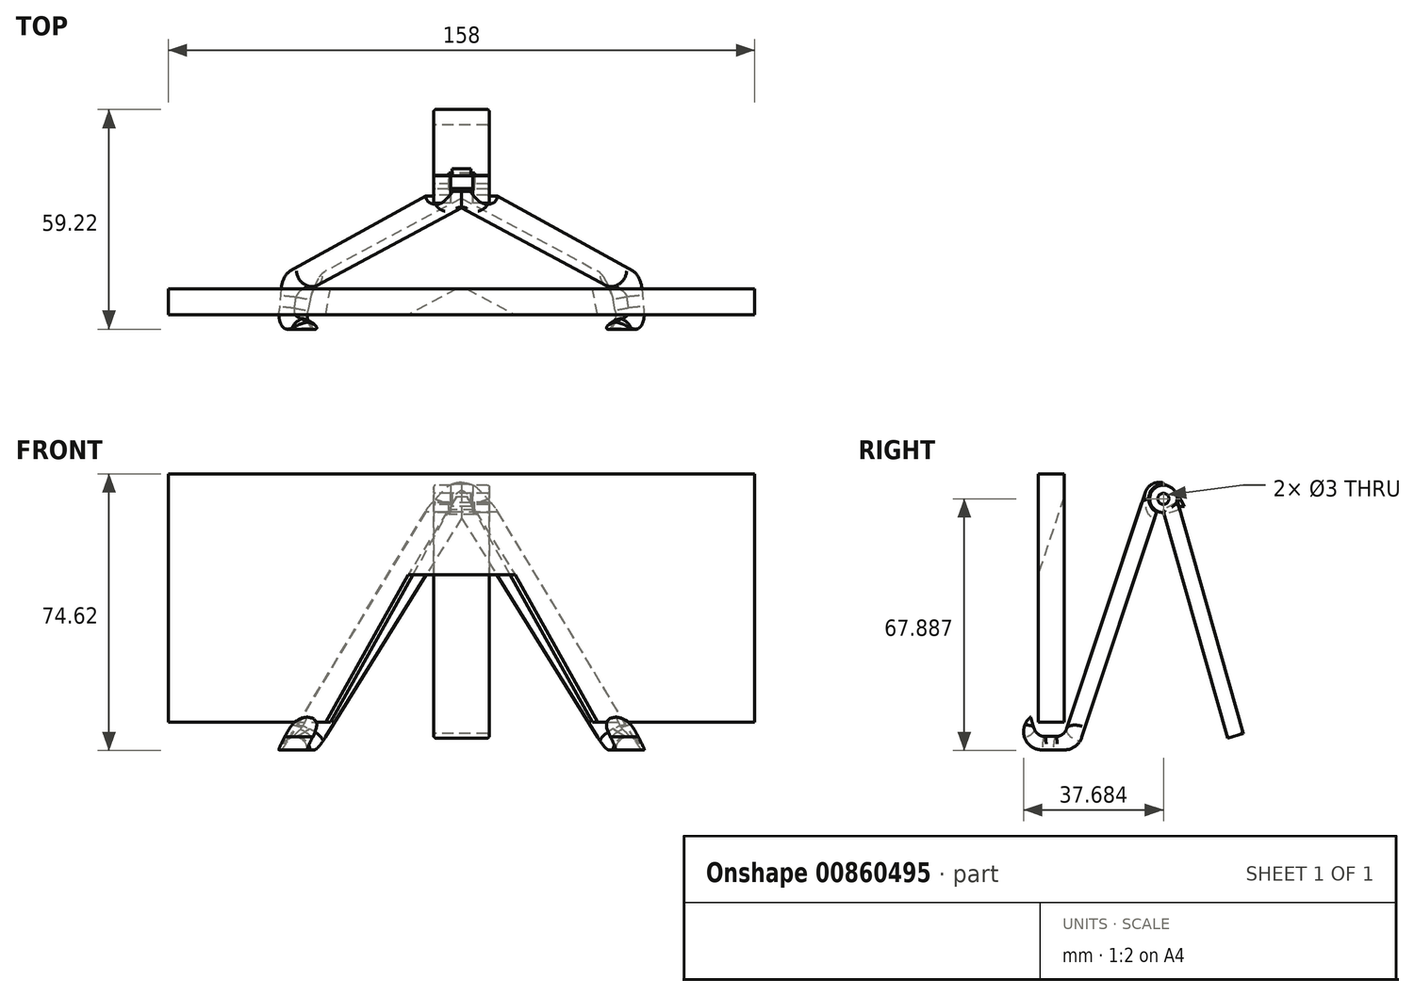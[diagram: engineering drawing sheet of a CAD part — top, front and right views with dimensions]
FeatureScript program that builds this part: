
annotation { "Feature Type Name" : "Feature", "Feature Type Description" : "" }
export const myFeature = defineFeature(function(context is Context, id is Id, definition is map)
    precondition{}
    {
        {
            var Q0;
            Q0=qCreatedBy(makeId("Front.planeOp"),FACE);
            var sketch = newSketch(context, id + "F0", { "sketchPlane" : qUnion([Q0])});
            skLineSegment(sketch, "E0.bottom", {"start": v(-79, 33.5) * mm, "end": v(79, 33.5) * mm});
            skLineSegment(sketch, "E0.top", {"start": v(-79, -33.5) * mm, "end": v(79, -33.5) * mm});
            skLineSegment(sketch, "E0.left", {"start": v(-79, 33.5) * mm, "end": v(-79, -33.5) * mm});
            skLineSegment(sketch, "E0.right", {"start": v(79, 33.5) * mm, "end": v(79, -33.5) * mm});
            skPoint(sketch, "E0.middle", {"position": v(0, 0) * mm});
            skSolve(sketch);
        }
        {
            var Q0;
            Q0=makeQuery(id+"F0.imprint","IMPRINT",FACE,{"disambiguationData":[TD([[makeQuery(id+"F0.imprint","IMPRINT",EDGE,{"derivedFrom":sQuery(id+"F0.wireOp",EDGE,"E0.bottom")}),-1.0]])]});
            extrude(context, id + "F1", {"entities" : qUnion([Q0]), "depth" : 7 * mm, "offsetDistance" : 25 * mm});
        }
        {
            var Q0;
            Q0=qCreatedBy(makeId("Right.planeOp"),FACE);
            var sketch = newSketch(context, id + "F2", { "sketchPlane" : qUnion([Q0])});
            skLineSegment(sketch, "E1", {"start": v(-9.07, -31.74) * mm, "end": v(-7.37, -37.3) * mm});
            skLineSegment(sketch, "E2", {"start": v(-7.37, -37.3) * mm, "end": v(0, -37.3) * mm});
            skLineSegment(sketch, "E3", {"start": v(0, -37.3) * mm, "end": v(22.96, 31.77) * mm});
            skLineSegment(sketch, "E4", {"start": v(-9.07, -31.74) * mm, "end": v(-12.14, -32.68) * mm});
            skLineSegment(sketch, "E5", {"start": v(-12.14, -32.68) * mm, "end": v(-9.6, -40.94) * mm});
            skLineSegment(sketch, "E6", {"start": v(-9.6, -40.94) * mm, "end": v(3.65, -40.94) * mm});
            skLineSegment(sketch, "E7", {"start": v(3.65, -40.94) * mm, "end": v(27.56, 30.98) * mm});
            skLineSegment(sketch, "E8", {"start": v(27.56, 30.98) * mm, "end": v(22.96, 31.77) * mm});
            skLineSegment(sketch, "E9", {"start": v(-7.37, -37.3) * mm, "end": v(-9.6, -40.94) * mm});
            skLineSegment(sketch, "E10", {"start": v(3.97, -25.36) * mm, "end": v(7.92, -28.08) * mm});
            skSolve(sketch);
        }
        {
            var Q0;
            {var subQ0=sQuery(id+"F2.wireOp",EDGE,"E8");Q0=makeQuery(id+"F2.imprint","IMPRINT",FACE,{"disambiguationData":[TD([[makeQuery(id+"F2.imprint","IMPRINT",EDGE,{"derivedFrom":subQ0}),1.0]])]});}
            var Q1;
            Q1=makeQuery(id+"F2.imprint","IMPRINT",FACE,{"disambiguationData":[TD([[makeQuery(id+"F2.imprint","IMPRINT",EDGE,{"derivedFrom":sQuery(id+"F2.wireOp",EDGE,"E1")}),-1.0]])]});
            var Q2;
            {var subQ4=sQuery(id+"F2.wireOp",EDGE,"E2");Q2=makeQuery(id+"F2.imprint","IMPRINT",FACE,{"disambiguationData":[TD([[makeQuery(id+"F2.imprint","IMPRINT",EDGE,{"derivedFrom":subQ4}),-1.0]])]});}
            extrude(context, id + "F3", {"entities" : qUnion([Q0, Q1, Q2]), "endBound" : BoundingType.SYMMETRIC, "depth" : 100 * mm, "offsetDistance" : 25 * mm});
        }
        {
            var Q0;
            Q0=makeQuery(id+"F3.opExtrude","SWEPT_FACE",FACE,{"disambiguationData":[OSD([sQuery(id+"F2.wireOp",EDGE,"E7")])]});
            var sketch = newSketch(context, id + "F4", { "sketchPlane" : qUnion([Q0])});
            skLineSegment(sketch, "E11", {"start": v(0, 0) * mm, "end": v(0, 28.2) * mm});
            skPoint(sketch, "E11.endSnap0", {"position": v(0, 38.1) * mm});
            skLineSegment(sketch, "E12", {"start": v(0, 28.2) * mm, "end": v(42.66, -44.2) * mm});
            skLineSegment(sketch, "E13", {"start": v(42.66, -44.2) * mm, "end": v(0, -44.2) * mm});
            skLineSegment(sketch, "E14", {"start": v(0, -44.2) * mm, "end": v(0, 0) * mm});
            skLineSegment(sketch, "E15.MirrorCS", {"start": v(0, 28.2) * mm, "end": v(-42.66, -44.2) * mm});
            skLineSegment(sketch, "E16.MirrorCS", {"start": v(-42.66, -44.2) * mm, "end": v(0, -44.2) * mm});
            skSolve(sketch);
        }
        {
            var Q0;
            {var subQ0=sQuery(id+"F4.wireOp",EDGE,"E11");Q0=makeQuery(id+"F4.imprint","IMPRINT",FACE,{"disambiguationData":[TD([[makeQuery(id+"F4.imprint","IMPRINT",EDGE,{"derivedFrom":subQ0}),1.0]])]});}
            var Q1;
            {var subQ0=sQuery(id+"F4.wireOp",EDGE,"E11");Q1=makeQuery(id+"F4.imprint","IMPRINT",FACE,{"disambiguationData":[TD([[makeQuery(id+"F4.imprint","IMPRINT",EDGE,{"derivedFrom":subQ0}),-1.0]])]});}
            var Q2;
            {var subQ0=sQuery(id+"F4.wireOp",EDGE,"E13");Q2=makeQuery(id+"F4.imprint","IMPRINT",FACE,{"disambiguationData":[TD([[makeQuery(id+"F4.imprint","IMPRINT",EDGE,{"derivedFrom":subQ0}),-1.0]])]});}
            var Q3;
            {var subQ0=sQuery(id+"F4.wireOp",EDGE,"E16.MirrorCS");Q3=makeQuery(id+"F4.imprint","IMPRINT",FACE,{"disambiguationData":[TD([[makeQuery(id+"F4.imprint","IMPRINT",EDGE,{"derivedFrom":subQ0}),1.0]])]});}
            extrude(context, id + "F5", {"entities" : qUnion([Q0, Q1, Q2, Q3]), "operationType" : NewBodyOperationType.REMOVE, "oppositeDirection" : true, "depth" : 25 * mm, "offsetDistance" : 25 * mm});
        }
        {
            var Q0;
            Q0=makeQuery(id+"F3.opExtrude","CAP_EDGE",EDGE,{"disambiguationData":[OSD([sQuery(id+"F2.wireOp",EDGE,"E8")])],"isStart":true});
            var Q1;
            Q1=makeQuery(id+"F3.opExtrude","CAP_EDGE",EDGE,{"disambiguationData":[OSD([sQuery(id+"F2.wireOp",EDGE,"E8")])],"isStart":false});
            chamfer(context, id + "F6", {"entities" : qUnion([Q0, Q1]), "chamferType" : ChamferType.OFFSET_ANGLE, "width" : 45 * mm, "oppositeDirection" : false, "angle" : 60 * degree, "tangentPropagation" : true});
        }
        {
            var Q0;
            {var subQ0=sQuery(id+"F2.wireOp",EDGE,"E8");Q0=makeQuery(id+"F6.opChamfer","BLEND_EDGE",EDGE,{"blendedFrom":[makeQuery(id+"F3.opExtrude","CAP_EDGE",EDGE,{"disambiguationData":[OSD([subQ0])],"isStart":true}),makeQuery(id+"F3.opExtrude","SWEPT_FACE",FACE,{"disambiguationData":[OSD([subQ0])]})],"blendedInto":[makeQuery(id+"F3.opExtrude","SWEPT_FACE",FACE,{"disambiguationData":[OSD([subQ0])]})]});}
            var Q1;
            {var subQ0=sQuery(id+"F2.wireOp",EDGE,"E8");Q1=makeQuery(id+"F6.opChamfer","BLEND_EDGE",EDGE,{"blendedFrom":[makeQuery(id+"F3.opExtrude","CAP_EDGE",EDGE,{"disambiguationData":[OSD([subQ0])],"isStart":false}),makeQuery(id+"F3.opExtrude","SWEPT_FACE",FACE,{"disambiguationData":[OSD([subQ0])]})],"blendedInto":[makeQuery(id+"F3.opExtrude","SWEPT_FACE",FACE,{"disambiguationData":[OSD([subQ0])]})]});}
            fillet(context, id + "F7", {"entities" : qUnion([Q0, Q1]), "radius" : 10 * mm, "tangentPropagation" : true, "allowEdgeOverflow" : false});
        }
        {
            var Q0;
            Q0=qCreatedBy(makeId("Right.planeOp"),FACE);
            var sketch = newSketch(context, id + "F8", { "sketchPlane" : qUnion([Q0])});
            skCircle(sketch, "E17", {"center": v(26.8, 26.76) * mm, "radius": 1.5 * mm});
            skCircle(sketch, "E18.0", {"center": v(26.8, 26.76) * mm, "radius": 4 * mm});
            skLineSegment(sketch, "E19", {"start": v(30.5, 28.26) * mm, "end": v(32.38, 24.7) * mm});
            skLineSegment(sketch, "E20", {"start": v(32.38, 24.7) * mm, "end": v(30.25, 24.73) * mm});
            skSolve(sketch);
        }
        {
            var Q0;
            Q0=makeQuery(id+"F8.imprint","IMPRINT",FACE,{"disambiguationData":[TD([[makeQuery(id+"F8.imprint","IMPRINT",EDGE,{"derivedFrom":sQuery(id+"F8.wireOp",EDGE,"E17")}),-1.0]])]});
            var Q1;
            {var subQ0=sQuery(id+"F8.wireOp",EDGE,"E19");Q1=makeQuery(id+"F8.imprint","IMPRINT",FACE,{"disambiguationData":[TD([[makeQuery(id+"F8.imprint","IMPRINT",EDGE,{"derivedFrom":subQ0}),-1.0]])]});}
            extrude(context, id + "F9", {"entities" : qUnion([Q0, Q1]), "endBound" : BoundingType.SYMMETRIC, "depth" : 5 * mm, "offsetDistance" : 25 * mm});
        }
        {
            var Q0;
            Q0=makeQuery(id+"F8.imprint","IMPRINT",FACE,{"disambiguationData":[TD([[makeQuery(id+"F8.imprint","IMPRINT",EDGE,{"derivedFrom":sQuery(id+"F8.wireOp",EDGE,"E17")}),1.0]])]});
            extrude(context, id + "F10", {"entities" : qUnion([Q0]), "operationType" : NewBodyOperationType.REMOVE, "endBound" : BoundingType.SYMMETRIC, "oppositeDirection" : true, "depth" : 25 * mm, "offsetDistance" : 25 * mm});
        }
        {
            var Q0;
            Q0=qCreatedBy(makeId("Right.planeOp"),FACE);
            var sketch = newSketch(context, id + "F11", { "sketchPlane" : qUnion([Q0])});
            skCircle(sketch, "E21", {"center": v(26.8, 26.77) * mm, "radius": 1.5 * mm});
            skCircle(sketch, "E22.0", {"center": v(26.8, 26.77) * mm, "radius": 3.7 * mm});
            skSolve(sketch);
        }
        {
            var Q0;
            Q0=makeQuery(id+"F8.imprint","IMPRINT",FACE,{"disambiguationData":[TD([[makeQuery(id+"F8.imprint","IMPRINT",EDGE,{"derivedFrom":sQuery(id+"F8.wireOp",EDGE,"E17")}),-1.0]])]});
            extrude(context, id + "F12", {"entities" : qUnion([Q0]), "operationType" : NewBodyOperationType.REMOVE, "endBound" : BoundingType.SYMMETRIC, "depth" : 25 * mm, "offsetDistance" : 25 * mm});
        }
        {
            var Q0;
            Q0=makeQuery(id+"F11.imprint","IMPRINT",FACE,{"disambiguationData":[TD([[makeQuery(id+"F11.imprint","IMPRINT",EDGE,{"derivedFrom":sQuery(id+"F11.wireOp",EDGE,"E21")}),-1.0]])]});
            extrude(context, id + "F13", {"entities" : qUnion([Q0]), "endBound" : BoundingType.SYMMETRIC, "depth" : 15 * mm, "offsetDistance" : 25 * mm});
        }
        {
            var Q0;
            Q0=qCreatedBy(makeId("Right.planeOp"),FACE);
            var sketch = newSketch(context, id + "F14", { "sketchPlane" : qUnion([Q0])});
            skLineSegment(sketch, "E23", {"start": v(26.65, 23.91) * mm, "end": v(44.16, -37.71) * mm});
            skLineSegment(sketch, "E24", {"start": v(44.16, -37.71) * mm, "end": v(48.33, -36.53) * mm});
            skLineSegment(sketch, "E25", {"start": v(48.33, -36.53) * mm, "end": v(30.6, 25.84) * mm});
            skLineSegment(sketch, "E26", {"start": v(26.65, 23.91) * mm, "end": v(30.6, 25.84) * mm});
            skLineSegment(sketch, "E27", {"start": v(31.19, 23.8) * mm, "end": v(27.02, 22.62) * mm});
            skSolve(sketch);
        }
        {
            var Q0;
            Q0=makeQuery(id+"F11.imprint","IMPRINT",FACE,{"disambiguationData":[TD([[makeQuery(id+"F11.imprint","IMPRINT",EDGE,{"derivedFrom":sQuery(id+"F11.wireOp",EDGE,"E21")}),-1.0]])]});
            extrude(context, id + "F15", {"entities" : qUnion([Q0]), "operationType" : NewBodyOperationType.REMOVE, "endBound" : BoundingType.SYMMETRIC, "oppositeDirection" : true, "depth" : 6 * mm, "offsetDistance" : 25 * mm});
        }
        {
            var Q0;
            Q0=makeQuery(id+"F14.imprint","IMPRINT",FACE,{"disambiguationData":[TD([[makeQuery(id+"F14.imprint","IMPRINT",EDGE,{"derivedFrom":sQuery(id+"F14.wireOp",EDGE,"E23")}),1.0]])]});
            extrude(context, id + "F16", {"entities" : qUnion([Q0]), "operationType" : NewBodyOperationType.ADD, "endBound" : BoundingType.SYMMETRIC, "depth" : 15 * mm, "offsetDistance" : 25 * mm});
        }
        {
            var Q0;
            {var subQ0=sQuery(id+"F14.wireOp",EDGE,"E26");Q0=makeQuery(id+"F14.imprint","IMPRINT",FACE,{"disambiguationData":[TD([[makeQuery(id+"F14.imprint","IMPRINT",EDGE,{"derivedFrom":subQ0}),-1.0]])]});}
            extrude(context, id + "F17", {"entities" : qUnion([Q0]), "operationType" : NewBodyOperationType.REMOVE, "endBound" : BoundingType.SYMMETRIC, "depth" : 7 * mm, "offsetDistance" : 25 * mm});
        }
        {
            var Q0;
            {var subQ0=sQuery(id+"F2.wireOp",EDGE,"E8");Q0=makeQuery(id+"F7.opFillet","BLEND_EDGE",EDGE,{"blendedFrom":[makeQuery(id+"F6.opChamfer","BLEND_EDGE",EDGE,{"blendedFrom":[makeQuery(id+"F3.opExtrude","CAP_EDGE",EDGE,{"disambiguationData":[OSD([subQ0])],"isStart":true}),makeQuery(id+"F3.opExtrude","SWEPT_FACE",FACE,{"disambiguationData":[OSD([subQ0])]})],"blendedInto":[makeQuery(id+"F3.opExtrude","SWEPT_FACE",FACE,{"disambiguationData":[OSD([subQ0])]})]}),makeQuery(id+"F3.opExtrude","SWEPT_FACE",FACE,{"disambiguationData":[OSD([sQuery(id+"F2.wireOp",EDGE,"E7")])]})],"blendedInto":[makeQuery(id+"F3.opExtrude","SWEPT_FACE",FACE,{"disambiguationData":[OSD([sQuery(id+"F2.wireOp",EDGE,"E7")])]})]});}
            var Q1;
            {var subQ0=sQuery(id+"F2.wireOp",EDGE,"E8");Q1=makeQuery(id+"F7.opFillet","BLEND_EDGE",EDGE,{"blendedFrom":[makeQuery(id+"F6.opChamfer","BLEND_EDGE",EDGE,{"blendedFrom":[makeQuery(id+"F3.opExtrude","CAP_EDGE",EDGE,{"disambiguationData":[OSD([subQ0])],"isStart":false}),makeQuery(id+"F3.opExtrude","SWEPT_FACE",FACE,{"disambiguationData":[OSD([subQ0])]})],"blendedInto":[makeQuery(id+"F3.opExtrude","SWEPT_FACE",FACE,{"disambiguationData":[OSD([subQ0])]})]}),makeQuery(id+"F3.opExtrude","SWEPT_FACE",FACE,{"disambiguationData":[OSD([sQuery(id+"F2.wireOp",EDGE,"E7")])]})],"blendedInto":[makeQuery(id+"F3.opExtrude","SWEPT_FACE",FACE,{"disambiguationData":[OSD([sQuery(id+"F2.wireOp",EDGE,"E7")])]})]});}
            fillet(context, id + "F18", {"entities" : qUnion([Q0, Q1]), "radius" : 1 * mm, "tangentPropagation" : true, "allowEdgeOverflow" : false});
        }
        {
            var Q0;
            Q0=makeQuery(id+"F16.boolean.opBoolean","MERGE",FACE,{"derivedFrom":[makeQuery(id+"F13.opExtrude","CAP_FACE",FACE,{"disambiguationData":[OSD([sQuery(id+"F11.wireOp",EDGE,"E21"),sQuery(id+"F11.wireOp",EDGE,"E22.0")])],"isStart":true}),makeQuery(id+"F16.opExtrude","CAP_FACE",FACE,{"disambiguationData":[OSD([sQuery(id+"F14.wireOp",EDGE,"E23"),sQuery(id+"F14.wireOp",EDGE,"E24"),sQuery(id+"F14.wireOp",EDGE,"E25"),sQuery(id+"F14.wireOp",EDGE,"E26")])],"isStart":true})]});
            var Q1;
            Q1=makeQuery(id+"F16.boolean.opBoolean","MERGE",FACE,{"derivedFrom":[makeQuery(id+"F13.opExtrude","CAP_FACE",FACE,{"disambiguationData":[OSD([sQuery(id+"F11.wireOp",EDGE,"E21"),sQuery(id+"F11.wireOp",EDGE,"E22.0")])],"isStart":false}),makeQuery(id+"F16.opExtrude","CAP_FACE",FACE,{"disambiguationData":[OSD([sQuery(id+"F14.wireOp",EDGE,"E23"),sQuery(id+"F14.wireOp",EDGE,"E24"),sQuery(id+"F14.wireOp",EDGE,"E25"),sQuery(id+"F14.wireOp",EDGE,"E26")])],"isStart":false})]});
            fillet(context, id + "F19", {"entities" : qUnion([Q0, Q1]), "radius" : .5 * mm, "tangentPropagation" : true, "allowEdgeOverflow" : false});
        }
        {
            var Q0;
            {var subQ0=sQuery(id+"F2.wireOp",EDGE,"E3");var subQ1=sQuery(id+"F2.wireOp",EDGE,"E2");Q0=makeQuery(id+"F5.boolean.opBoolean","SPLIT",EDGE,{"disambiguationData":[TD([makeQuery(id+"F5.opExtrude","SWEPT_FACE",FACE,{"disambiguationData":[OSD([sQuery(id+"F4.wireOp",EDGE,"E12")])]})])],"derivedFrom":makeQuery(id+"F3.opExtrude","SWEPT_EDGE",EDGE,{"disambiguationData":[OSD([subQ1,subQ0])]})});}
            var Q1;
            {var subQ0=sQuery(id+"F2.wireOp",EDGE,"E1");var subQ1=sQuery(id+"F2.wireOp",EDGE,"E2");Q1=makeQuery(id+"F5.boolean.opBoolean","SPLIT",EDGE,{"disambiguationData":[TD([makeQuery(id+"F5.opExtrude","SWEPT_FACE",FACE,{"disambiguationData":[OSD([sQuery(id+"F4.wireOp",EDGE,"E12")])]})])],"derivedFrom":makeQuery(id+"F3.opExtrude","SWEPT_EDGE",EDGE,{"disambiguationData":[OSD([subQ0,subQ1,sQuery(id+"F2.wireOp",EDGE,"E9")])]})});}
            var Q2;
            {var subQ0=sQuery(id+"F2.wireOp",EDGE,"E3");var subQ1=sQuery(id+"F2.wireOp",EDGE,"E2");Q2=makeQuery(id+"F5.boolean.opBoolean","SPLIT",EDGE,{"disambiguationData":[TD([makeQuery(id+"F5.opExtrude","SWEPT_FACE",FACE,{"disambiguationData":[OSD([sQuery(id+"F4.wireOp",EDGE,"E15.MirrorCS")])]})])],"derivedFrom":makeQuery(id+"F3.opExtrude","SWEPT_EDGE",EDGE,{"disambiguationData":[OSD([subQ1,subQ0])]})});}
            var Q3;
            {var subQ0=sQuery(id+"F2.wireOp",EDGE,"E1");var subQ1=sQuery(id+"F2.wireOp",EDGE,"E2");Q3=makeQuery(id+"F5.boolean.opBoolean","SPLIT",EDGE,{"disambiguationData":[TD([makeQuery(id+"F5.opExtrude","SWEPT_FACE",FACE,{"disambiguationData":[OSD([sQuery(id+"F4.wireOp",EDGE,"E15.MirrorCS")])]})])],"derivedFrom":makeQuery(id+"F3.opExtrude","SWEPT_EDGE",EDGE,{"disambiguationData":[OSD([subQ0,subQ1,sQuery(id+"F2.wireOp",EDGE,"E9")])]})});}
            fillet(context, id + "F20", {"entities" : qUnion([Q0, Q1, Q2, Q3]), "radius" : 3 * mm, "tangentPropagation" : true, "allowEdgeOverflow" : false});
        }
        {
            var Q0;
            Q0=makeQuery(id+"F6.opChamfer","BLEND_EDGE",EDGE,{"blendedFrom":[makeQuery(id+"F3.opExtrude","CAP_EDGE",EDGE,{"disambiguationData":[OSD([sQuery(id+"F2.wireOp",EDGE,"E8")])],"isStart":false}),makeQuery(id+"F3.opExtrude","SWEPT_FACE",FACE,{"disambiguationData":[OSD([sQuery(id+"F2.wireOp",EDGE,"E3")])]})],"blendedInto":[makeQuery(id+"F3.opExtrude","SWEPT_FACE",FACE,{"disambiguationData":[OSD([sQuery(id+"F2.wireOp",EDGE,"E3")])]})]});
            var Q1;
            Q1=makeQuery(id+"F3.opExtrude","SWEPT_FACE",FACE,{"disambiguationData":[OSD([sQuery(id+"F2.wireOp",EDGE,"E3")])]});
            var Q2;
            {var subQ0=sQuery(id+"F2.wireOp",EDGE,"E8");Q2=makeQuery(id+"F7.opFillet","BLEND_EDGE",EDGE,{"blendedFrom":[makeQuery(id+"F6.opChamfer","BLEND_EDGE",EDGE,{"blendedFrom":[makeQuery(id+"F3.opExtrude","CAP_EDGE",EDGE,{"disambiguationData":[OSD([subQ0])],"isStart":true}),makeQuery(id+"F3.opExtrude","SWEPT_FACE",FACE,{"disambiguationData":[OSD([subQ0])]})],"blendedInto":[makeQuery(id+"F3.opExtrude","SWEPT_FACE",FACE,{"disambiguationData":[OSD([subQ0])]})]}),makeQuery(id+"F3.opExtrude","SWEPT_FACE",FACE,{"disambiguationData":[OSD([sQuery(id+"F2.wireOp",EDGE,"E3")])]})],"blendedInto":[makeQuery(id+"F3.opExtrude","SWEPT_FACE",FACE,{"disambiguationData":[OSD([sQuery(id+"F2.wireOp",EDGE,"E3")])]})]});}
            fillet(context, id + "F21", {"entities" : qUnion([Q0, Q1, Q2]), "radius" : 4 * mm, "tangentPropagation" : true, "allowEdgeOverflow" : false});
        }
        {
            var Q0;
            {var subQ0=sQuery(id+"F2.wireOp",EDGE,"E6");var subQ1=sQuery(id+"F2.wireOp",EDGE,"E5");Q0=makeQuery(id+"F5.boolean.opBoolean","SPLIT",EDGE,{"disambiguationData":[TD([makeQuery(id+"F5.opExtrude","SWEPT_FACE",FACE,{"disambiguationData":[OSD([sQuery(id+"F4.wireOp",EDGE,"E15.MirrorCS")])]})])],"derivedFrom":makeQuery(id+"F3.opExtrude","SWEPT_EDGE",EDGE,{"disambiguationData":[OSD([subQ1,subQ0,sQuery(id+"F2.wireOp",EDGE,"E9")])]})});}
            var Q1;
            {var subQ0=sQuery(id+"F2.wireOp",EDGE,"E7");var subQ1=sQuery(id+"F2.wireOp",EDGE,"E6");Q1=makeQuery(id+"F5.boolean.opBoolean","SPLIT",EDGE,{"disambiguationData":[TD([makeQuery(id+"F5.opExtrude","SWEPT_FACE",FACE,{"disambiguationData":[OSD([sQuery(id+"F4.wireOp",EDGE,"E15.MirrorCS")])]})])],"derivedFrom":makeQuery(id+"F3.opExtrude","SWEPT_EDGE",EDGE,{"disambiguationData":[OSD([subQ1,subQ0])]})});}
            var Q2;
            {var subQ0=sQuery(id+"F2.wireOp",EDGE,"E7");var subQ1=sQuery(id+"F2.wireOp",EDGE,"E6");Q2=makeQuery(id+"F5.boolean.opBoolean","SPLIT",EDGE,{"disambiguationData":[TD([makeQuery(id+"F5.opExtrude","SWEPT_FACE",FACE,{"disambiguationData":[OSD([sQuery(id+"F4.wireOp",EDGE,"E12")])]})])],"derivedFrom":makeQuery(id+"F3.opExtrude","SWEPT_EDGE",EDGE,{"disambiguationData":[OSD([subQ1,subQ0])]})});}
            var Q3;
            {var subQ0=sQuery(id+"F2.wireOp",EDGE,"E6");var subQ1=sQuery(id+"F2.wireOp",EDGE,"E5");Q3=makeQuery(id+"F5.boolean.opBoolean","SPLIT",EDGE,{"disambiguationData":[TD([makeQuery(id+"F5.opExtrude","SWEPT_FACE",FACE,{"disambiguationData":[OSD([sQuery(id+"F4.wireOp",EDGE,"E12")])]})])],"derivedFrom":makeQuery(id+"F3.opExtrude","SWEPT_EDGE",EDGE,{"disambiguationData":[OSD([subQ1,subQ0,sQuery(id+"F2.wireOp",EDGE,"E9")])]})});}
            fillet(context, id + "F22", {"entities" : qUnion([Q0, Q1, Q2, Q3]), "radius" : 5 * mm, "tangentPropagation" : true, "allowEdgeOverflow" : false});
        }
        {
            var Q0;
            {var subQ0=sQuery(id+"F2.wireOp",EDGE,"E5");var subQ1=sQuery(id+"F2.wireOp",EDGE,"E4");Q0=makeQuery(id+"F5.boolean.opBoolean","SPLIT",EDGE,{"disambiguationData":[TD([makeQuery(id+"F5.opExtrude","SWEPT_FACE",FACE,{"disambiguationData":[OSD([sQuery(id+"F4.wireOp",EDGE,"E15.MirrorCS")])]})])],"derivedFrom":makeQuery(id+"F3.opExtrude","SWEPT_EDGE",EDGE,{"disambiguationData":[OSD([subQ1,subQ0])]})});}
            var Q1;
            {var subQ0=sQuery(id+"F2.wireOp",EDGE,"E5");var subQ1=sQuery(id+"F2.wireOp",EDGE,"E4");Q1=makeQuery(id+"F5.boolean.opBoolean","SPLIT",EDGE,{"disambiguationData":[TD([makeQuery(id+"F5.opExtrude","SWEPT_FACE",FACE,{"disambiguationData":[OSD([sQuery(id+"F4.wireOp",EDGE,"E12")])]})])],"derivedFrom":makeQuery(id+"F3.opExtrude","SWEPT_EDGE",EDGE,{"disambiguationData":[OSD([subQ1,subQ0])]})});}
            fillet(context, id + "F23", {"entities" : qUnion([Q0, Q1]), "radius" : 5 * mm, "tangentPropagation" : true, "allowEdgeOverflow" : false});
        }
    });
